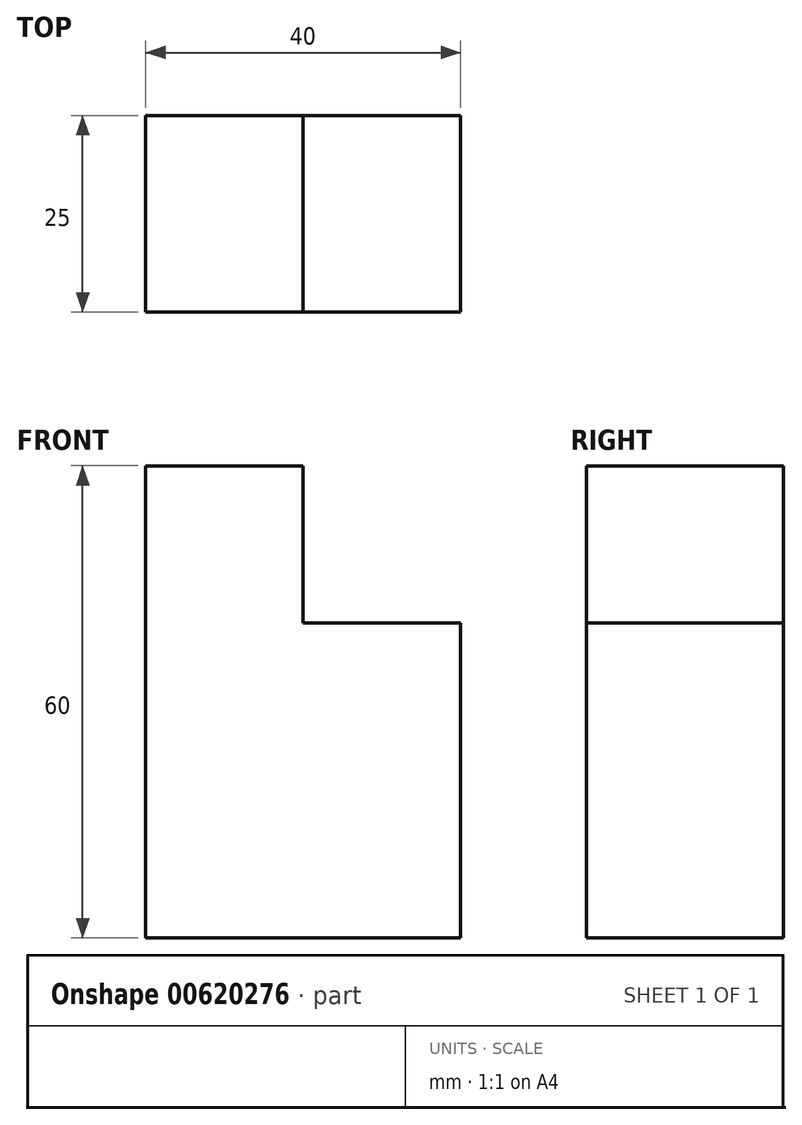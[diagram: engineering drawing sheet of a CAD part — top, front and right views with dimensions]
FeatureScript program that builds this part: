
annotation { "Feature Type Name" : "Feature", "Feature Type Description" : "" }
export const myFeature = defineFeature(function(context is Context, id is Id, definition is map)
    precondition{}
    {
        {
            var Q0;
            Q0=qCreatedBy(makeId("Front.planeOp"),FACE);
            var sketch = newSketch(context, id + "F0", { "sketchPlane" : qUnion([Q0])});
            skLineSegment(sketch, "E0", {"start": v(-20, 43.09) * mm, "end": v(-20, -16.91) * mm});
            skLineSegment(sketch, "E1", {"start": v(-20, -16.91) * mm, "end": v(20, -16.91) * mm});
            skLineSegment(sketch, "E2", {"start": v(20, -16.91) * mm, "end": v(20, 23.09) * mm});
            skLineSegment(sketch, "E3", {"start": v(20, 23.09) * mm, "end": v(0, 23.09) * mm});
            skLineSegment(sketch, "E4", {"start": v(0, 23.09) * mm, "end": v(0, 43.09) * mm});
            skLineSegment(sketch, "E5", {"start": v(-20, 43.09) * mm, "end": v(0, 43.09) * mm});
            skSolve(sketch);
        }
        {
            var Q0;
            Q0 = qSketchRegion(id + "F0", true);
            extrude(context, id + "F1", {"entities" : qUnion([Q0]), "depth" : 25 * mm, "offsetDistance" : 25 * mm});
        }
    });
